# Revit family: Chair-Multi_Purpose-Allermuir-Sholes-SHL01
name_source: partatom
category: Furniture
revit_build: Autodesk Revit MEP 2012 (Build: 20110309_2315)
units: mm (PartAtom-declared; Revit-internal decimal feet)

## types (1)
- SHL01
    04 CSI = 12 51 00
    95 CSI = 12510
    Assembly Code = E2020200
    Back Rest = Fabric - Allermuir - Blue
    Bag hook = Yes
    Base = Metal - Allermuir - Stainless Steel
    Color Availability = See price list for material options
    Cup Holder = Plastic - Allermuir - Nylon
    Cup Holder Visibility = Yes
    Default Elevation = 48 "
    Description = Side chair with skid base
    Glides = Plasticl - Allermuir - White
    Manufacturer = Allermuir
    Manufacturer Fax = (419) 887 5805
    Model = SHL01
    Overall Depth = 32 "
    Overall Height = 29 "
    Overall Width = 32 "
    Plastic Arms in Black = No
    Plastic glides = Yes
    Product Line = Sholes
    Rod = Metal - Allermuir - Stainless Steel
    Seat = Fabric - Allermuir - Blue
    Seat Depth = 0 "
    Seat Height = 0 "
    Seat Width = 0 "
    Seat or Base = Fabric - Allermuir - Blue
    Stacks = Yes
    Subcategory = Multi-Purpose
    Support = Metal - Allermuir - Stainless Steel
    Support Rod = Metal - Allermuir - Stainless Steel
    Suspension Rubber = Plastic - Allermuir - Black
    Tablet Base = Metal - Allermuir - Stainless Steel
    Weight = 0.0 lb
    Writing Tablet = Plastic - Allermuir - Smooth Black
    Writing Tablet Visibility = Yes
    Writing tablet = Plastic - Allermuir - Smooth Black
    Writing tablet Visibility = Yes

## geometry (parser evidence)
native form markers: Sweep x2
no freeform markers — native parametric forms only
